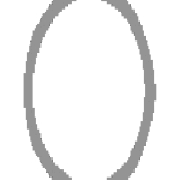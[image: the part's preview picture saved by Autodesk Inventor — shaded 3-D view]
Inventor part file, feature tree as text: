
AUTODESK INVENTOR PART (.ipt)
format: ipt  version: 2021 (Build 250183000, 183)  size: 114,688 bytes
history: native  units: in
note: dims shown in document units (in); Inventor stores cm internally (conversion verified against a paired STEP export)
features: other x4, sketch x3, plane x1
ambient origin geometry x8: Origin, YZ Plane, XZ Plane, XY Plane, X Axis, Y Axis, Z Axis, Center Point
bodies: Solid1 (feature_tree), Body (feature_tree)
feature tree (8):
  other  "Driven Length"
  other  "Frame Generator"
  other  "Start Plane"
  other  "End Plane"
  sketch  "Sketch"  dims[d2=6.0828in d4=-0.0in d5=6.0828in d6=0.12in d7=0.0in d8=90.0deg d9=6.0828in]
  sketch  "Sketch2"  dims[d0=1.0in]
  plane  "Work Plane3"
  sketch  "Sketch3"  dims[d1=0.065in]
